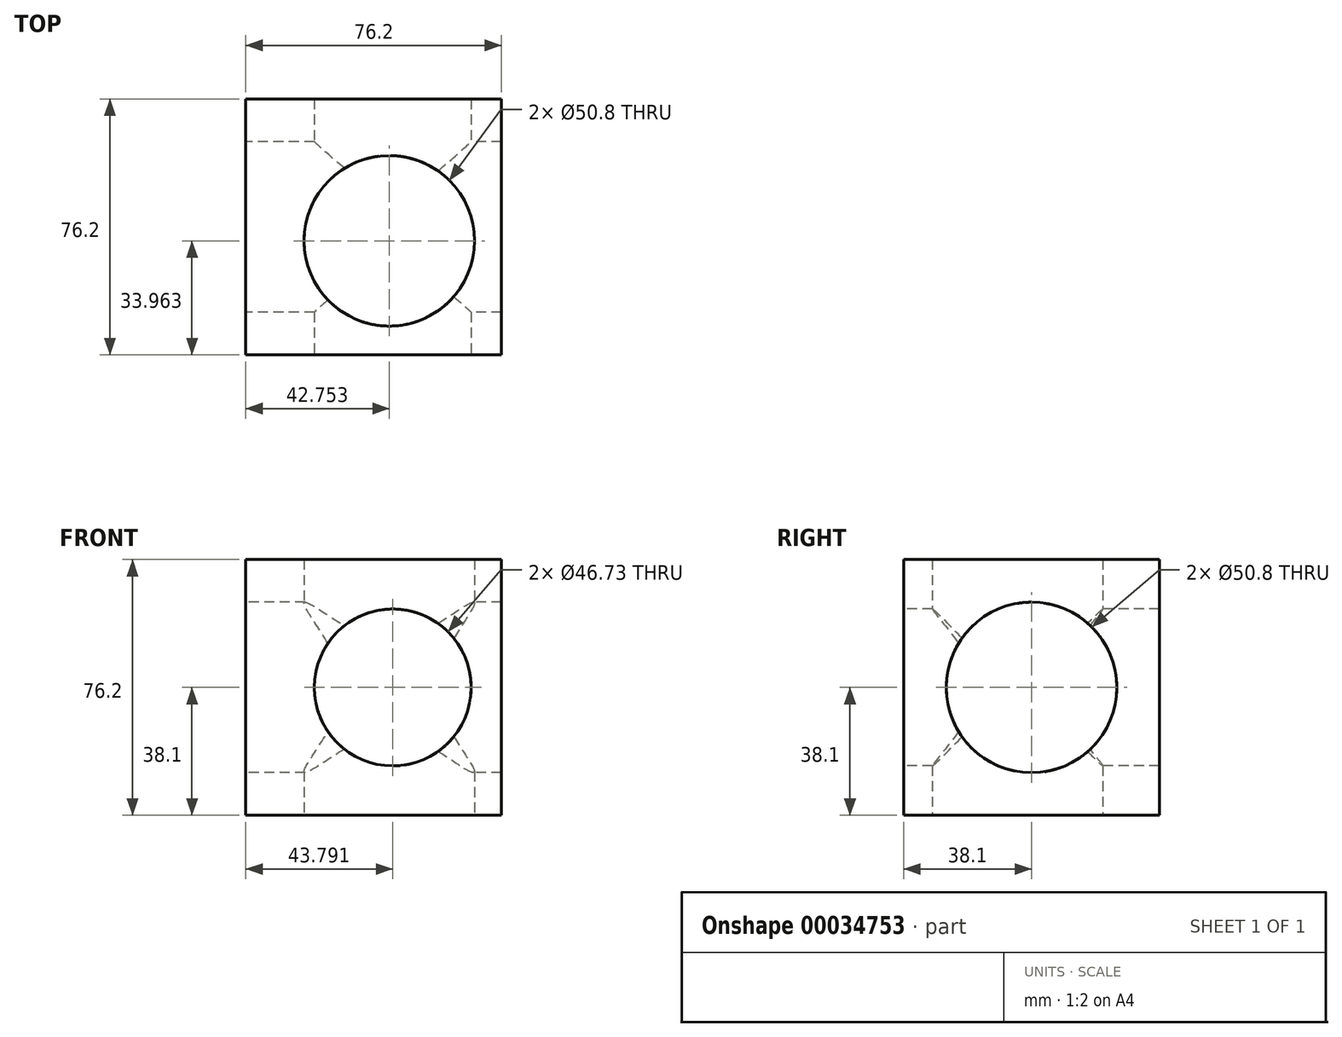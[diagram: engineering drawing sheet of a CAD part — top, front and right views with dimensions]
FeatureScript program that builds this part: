
annotation { "Feature Type Name" : "Feature", "Feature Type Description" : "" }
export const myFeature = defineFeature(function(context is Context, id is Id, definition is map)
    precondition{}
    {
        {
            var Q0;
            Q0=qCreatedBy(makeId("Front.planeOp"),FACE);
            var sketch = newSketch(context, id + "F0", { "sketchPlane" : qUnion([Q0])});
            skLineSegment(sketch, "E0.rect.bottom", {"start": v(38.1, -38.1) * mm, "end": v(-38.1, -38.1) * mm});
            skLineSegment(sketch, "E0.rect.top", {"start": v(38.1, 38.1) * mm, "end": v(-38.1, 38.1) * mm});
            skLineSegment(sketch, "E0.rect.left", {"start": v(38.1, -38.1) * mm, "end": v(38.1, 38.1) * mm});
            skLineSegment(sketch, "E0.rect.right", {"start": v(-38.1, -38.1) * mm, "end": v(-38.1, 38.1) * mm});
            skPoint(sketch, "E0.rect.middle", {"position": v(0, 0) * mm});
            skSolve(sketch);
        }
        {
            var Q0;
            Q0 = qSketchRegion(id + "F0", true);
            extrude(context, id + "F1", {"entities" : qUnion([Q0]), "endBound" : BoundingType.SYMMETRIC, "depth" : 76.2 * mm});
        }
        {
            var Q0;
            Q0=makeQuery(id+"F1.opExtrude","SWEPT_FACE",FACE,{"disambiguationData":[OSD([sQuery(id+"F0.wireOp",EDGE,"E0.rect.bottom")])]});
            var sketch = newSketch(context, id + "F2", { "sketchPlane" : qUnion([Q0])});
            skCircle(sketch, "E1", {"center": v(4.65, 4.14) * mm, "radius": 25.4 * mm});
            skSolve(sketch);
        }
        {
            var Q0;
            Q0 = qSketchRegion(id + "F2", true);
            extrude(context, id + "F3", {"entities" : qUnion([Q0]), "operationType" : NewBodyOperationType.REMOVE, "endBound" : BoundingType.THROUGH_ALL, "oppositeDirection" : true, "depth" : 25.4 * mm});
        }
        {
            var Q0;
            Q0=makeQuery(id+"F1.opExtrude","SWEPT_FACE",FACE,{"disambiguationData":[OSD([sQuery(id+"F0.wireOp",EDGE,"E0.rect.right")])]});
            var sketch = newSketch(context, id + "F4", { "sketchPlane" : qUnion([Q0])});
            skCircle(sketch, "E2", {"center": v(0, 0) * mm, "radius": 25.4 * mm});
            skSolve(sketch);
        }
        {
            var Q0;
            Q0 = qSketchRegion(id + "F4", true);
            extrude(context, id + "F5", {"entities" : qUnion([Q0]), "operationType" : NewBodyOperationType.REMOVE, "endBound" : BoundingType.THROUGH_ALL, "oppositeDirection" : true, "depth" : 25.4 * mm});
        }
        {
            var Q0;
            Q0=makeQuery(id+"F1.opExtrude","CAP_FACE",FACE,{"disambiguationData":[OSD([sQuery(id+"F0.wireOp",EDGE,"E0.rect.bottom"),sQuery(id+"F0.wireOp",EDGE,"E0.rect.top"),sQuery(id+"F0.wireOp",EDGE,"E0.rect.left"),sQuery(id+"F0.wireOp",EDGE,"E0.rect.right")])],"isStart":false});
            var sketch = newSketch(context, id + "F6", { "sketchPlane" : qUnion([Q0])});
            skCircle(sketch, "E3", {"center": v(5.7, 0) * mm, "radius": 23.36 * mm});
            skSolve(sketch);
        }
        {
            var Q0;
            Q0 = qSketchRegion(id + "F6", true);
            extrude(context, id + "F7", {"entities" : qUnion([Q0]), "operationType" : NewBodyOperationType.REMOVE, "endBound" : BoundingType.THROUGH_ALL, "oppositeDirection" : true, "depth" : 25.4 * mm});
        }
    });
